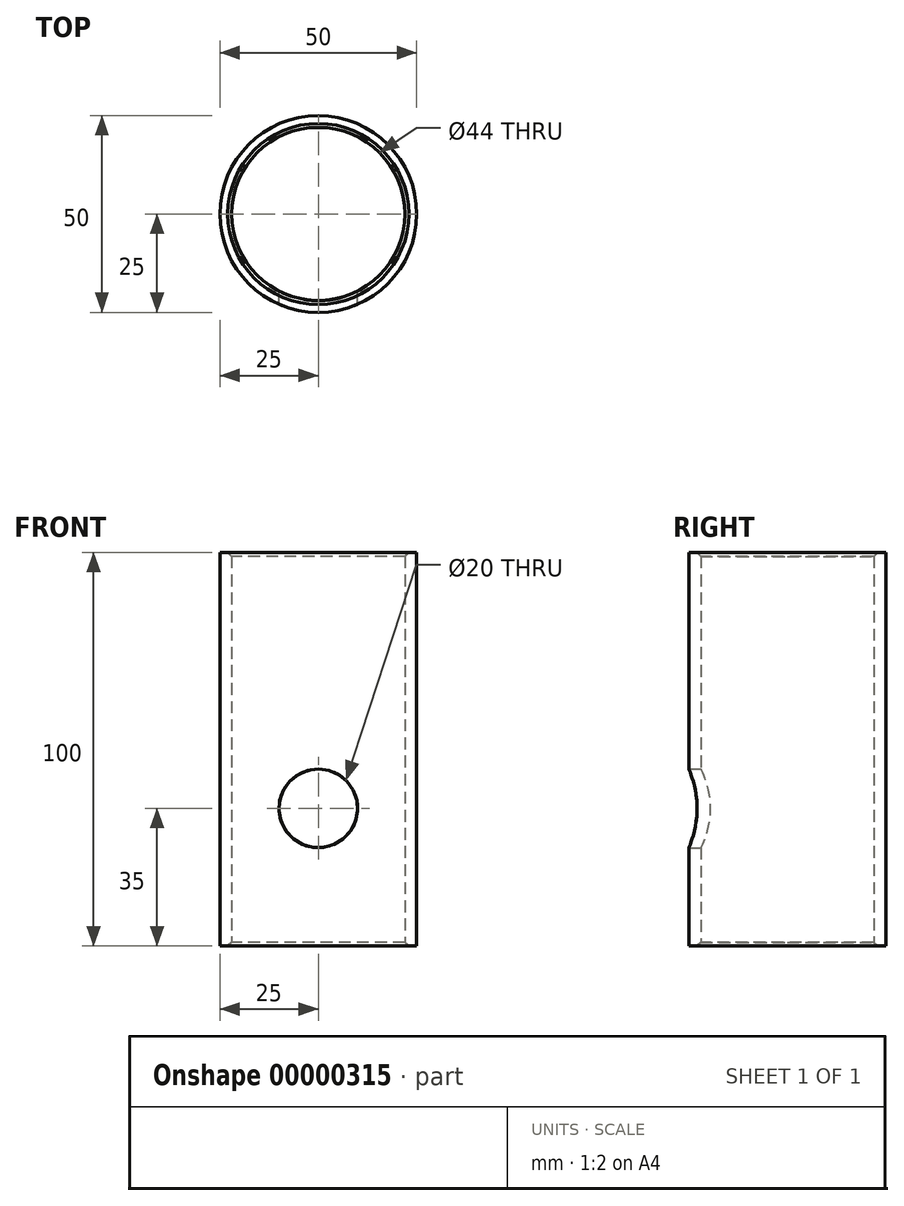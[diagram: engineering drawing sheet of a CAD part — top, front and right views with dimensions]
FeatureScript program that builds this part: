
annotation { "Feature Type Name" : "Feature", "Feature Type Description" : "" }
export const myFeature = defineFeature(function(context is Context, id is Id, definition is map)
    precondition{}
    {
        {
            var Q0;
            Q0=qCreatedBy(makeId("Front.planeOp"),FACE);
            var sketch = newSketch(context, id + "F0", { "sketchPlane" : qUnion([Q0])});
            skLineSegment(sketch, "E0", {"start": v(-53.08, 0) * mm, "end": v(53.08, 0) * mm, "construction": true});
            skSolve(sketch);
        }
        {
            var Q0;
            Q0=qCreatedBy(makeId("Top.planeOp"),FACE);
            var sketch = newSketch(context, id + "F1", { "sketchPlane" : qUnion([Q0])});
            skCircle(sketch, "E1", {"center": v(0, 0) * mm, "radius": 25 * mm});
            skSolve(sketch);
        }
        {
            var Q0;
            Q0=makeQuery(id+"F1.imprint","IMPRINT",FACE,{"disambiguationData":[TD([[makeQuery(id+"F1.imprint","IMPRINT",EDGE,{"derivedFrom":sQuery(id+"F1.wireOp",EDGE,"E1")}),1.0]])]});
            extrude(context, id + "F2", {"entities" : qUnion([Q0]), "endBound" : BoundingType.SYMMETRIC, "depth" : 100 * mm});
        }
        {
            var Q0;
            Q0=makeQuery(id+"F2.opExtrude","CAP_FACE",FACE,{"disambiguationData":[OSD([sQuery(id+"F1.wireOp",EDGE,"E1")])],"isStart":true});
            var Q1;
            Q1=makeQuery(id+"F2.opExtrude","CAP_FACE",FACE,{"disambiguationData":[OSD([sQuery(id+"F1.wireOp",EDGE,"E1")])],"isStart":false});
            shell(context, id + "F3", {"entities" : qUnion([Q0, Q1]), "thickness" : 3 * mm});
        }
        {
            var Q0;
            Q0=qCreatedBy(makeId("Front.planeOp"),FACE);
            var sketch = newSketch(context, id + "F4", { "sketchPlane" : qUnion([Q0])});
            skCircle(sketch, "E2", {"center": v(0, -15) * mm, "radius": 10 * mm});
            skCircle(sketch, "E3.0.MirrorC", {"center": v(0, 15) * mm, "radius": 10 * mm});
            skLineSegment(sketch, "E4.0", {"start": v(-25, -50) * mm, "end": v(25, -50) * mm, "construction": true});
            skSolve(sketch);
        }
        {
            var Q0;
            {Q0=qUnion([makeQuery(id+"F4.imprint","IMPRINT",FACE,{"disambiguationData":[TD([[makeQuery(id+"F4.imprint","IMPRINT",EDGE,{"derivedFrom":sQuery(id+"F4.wireOp",EDGE,"E2")}),1.0]])]}),makeQuery(id+"F4.imprint","IMPRINT",FACE,{"disambiguationData":[TD([[makeQuery(id+"F4.imprint","IMPRINT",EDGE,{"derivedFrom":sQuery(id+"F4.wireOp",EDGE,"E3.0.MirrorC")}),-1.0]])]})]);}
            extrude(context, id + "F5", {"entities" : qUnion([Q0]), "operationType" : NewBodyOperationType.REMOVE, "endBound" : BoundingType.THROUGH_ALL, "depth" : 25 * mm});
        }
        {
            var Q0;
            {var subQ0=sQuery(id+"F1.wireOp",EDGE,"E1");Q0=makeQuery(id+"F3.opShell","OFFSET_EDGE",EDGE,{"disambiguationData":[OSD([subQ0]),TDD([makeQuery(id+"F2.opExtrude","CAP_EDGE",EDGE,{"disambiguationData":[OSD([subQ0])],"isStart":false})])]});}
            var Q1;
            {var subQ0=sQuery(id+"F1.wireOp",EDGE,"E1");Q1=makeQuery(id+"F3.opShell","OFFSET_EDGE",EDGE,{"disambiguationData":[OSD([subQ0]),TDD([makeQuery(id+"F2.opExtrude","CAP_EDGE",EDGE,{"disambiguationData":[OSD([subQ0])],"isStart":true})])]});}
            chamfer(context, id + "F6", {"entities" : qUnion([Q0, Q1]), "width" : 1 * mm, "tangentPropagation" : true});
        }
    });
